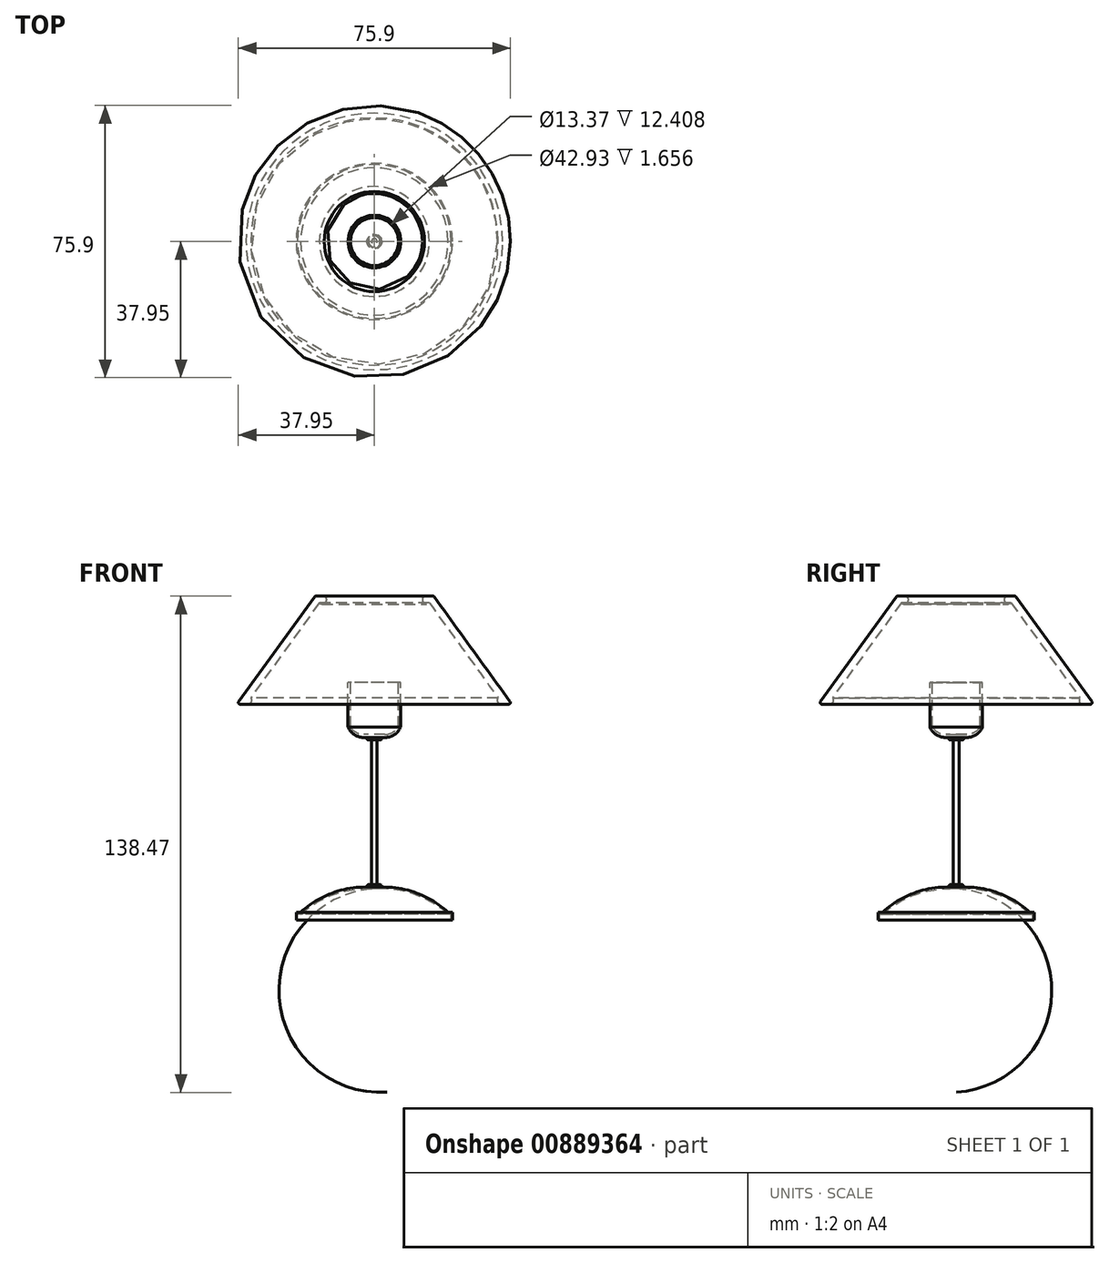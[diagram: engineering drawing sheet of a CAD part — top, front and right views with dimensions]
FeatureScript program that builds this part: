
annotation { "Feature Type Name" : "Feature", "Feature Type Description" : "" }
export const myFeature = defineFeature(function(context is Context, id is Id, definition is map)
    precondition{}
    {
        {
            var Q0;
            Q0=qCreatedBy(makeId("Front.planeOp"),FACE);
            var sketch = newSketch(context, id + "F0", { "sketchPlane" : qUnion([Q0])});
            skLineSegment(sketch, "E0", {"start": v(-13.97, 30.15) * mm, "end": v(-16.33, 30.15) * mm});
            skLineSegment(sketch, "E1", {"start": v(-16.7, 29.96) * mm, "end": v(-37.86, 0.73) * mm});
            skLineSegment(sketch, "E2", {"start": v(-37.48, 0) * mm, "end": v(-35.8, 0) * mm});
            skLineSegment(sketch, "E3", {"start": v(0, 30.15) * mm, "end": v(0, 37.7) * mm});
            skLineSegment(sketch, "E4", {"start": v(-34.51, 1.77) * mm, "end": v(-15.35, 28.25) * mm});
            skArc(sketch, "E5", {"start": v(-15.35, 28.25) * mm, "mid": v(-13.62, 28.45) * mm, "end": v(-13.97, 30.15) * mm});
            skArc(sketch, "E6", {"start": v(-35.8, 0) * mm, "mid": v(-34.5, 0.42) * mm, "end": v(-34.51, 1.77) * mm});
            skPoint(sketch, "E7.visualSharp", {"position": v(-38.39, 0) * mm});
            skArc(sketch, "E7.filletArc", {"start": v(-37.86, 0.73) * mm, "mid": v(-37.9, 0.25) * mm, "end": v(-37.48, 0) * mm});
            skPoint(sketch, "E8.visualSharp", {"position": v(-16.57, 30.15) * mm});
            skArc(sketch, "E8.filletArc", {"start": v(-16.33, 30.15) * mm, "mid": v(-16.54, 30.1) * mm, "end": v(-16.7, 29.96) * mm});
            skLineSegment(sketch, "E9", {"start": v(0, 0) * mm, "end": v(0, -60.18) * mm});
            skLineSegment(sketch, "E10", {"start": v(-21.47, -60.18) * mm, "end": v(-21.8, -60.18) * mm});
            skLineSegment(sketch, "E11", {"start": v(-21.8, -60.18) * mm, "end": v(-21.8, -58.08) * mm});
            skLineSegment(sketch, "E12", {"start": v(-21.8, -58.08) * mm, "end": v(-20.55, -58.08) * mm});
            skLineSegment(sketch, "E13", {"start": v(0, -51.02) * mm, "end": v(0, -51.5) * mm});
            skLineSegment(sketch, "E14", {"start": v(0, -51.02) * mm, "end": v(-2.49, -51.02) * mm});
            skArc(sketch, "E15", {"start": v(-2.49, -51.02) * mm, "mid": v(-12.18, -52.85) * mm, "end": v(-20.55, -58.08) * mm});
            skLineSegment(sketch, "E16", {"start": v(0, -50.3) * mm, "end": v(-1.58, -50.3) * mm});
            skArc(sketch, "E17", {"start": v(-1.58, -50.3) * mm, "mid": v(-1.94, -50.66) * mm, "end": v(-1.58, -51.02) * mm});
            skLineSegment(sketch, "E18", {"start": v(-0.79, -50.3) * mm, "end": v(-0.79, -9.98) * mm});
            skLineSegment(sketch, "E19", {"start": v(-0.79, -9.98) * mm, "end": v(-1.71, -9.98) * mm});
            skArc(sketch, "E20", {"start": v(-1.71, -9.28) * mm, "mid": v(-2.06, -9.63) * mm, "end": v(-1.71, -9.98) * mm});
            skLineSegment(sketch, "E21", {"start": v(-7.36, 6.1) * mm, "end": v(-7.36, -6.35) * mm});
            skArc(sketch, "E22", {"start": v(-7.36, -6.35) * mm, "mid": v(-5.58, -8.48) * mm, "end": v(-2.92, -9.28) * mm});
            skLineSegment(sketch, "E23", {"start": v(-7.36, 6.1) * mm, "end": v(-6.69, 6.1) * mm});
            skLineSegment(sketch, "E24", {"start": v(-6.69, 6.1) * mm, "end": v(-6.69, -6.31) * mm});
            skLineSegment(sketch, "E25", {"start": v(-2.92, -8.43) * mm, "end": v(0, -8.43) * mm});
            skArc(sketch, "E26", {"start": v(-6.69, -6.31) * mm, "mid": v(-5.08, -7.87) * mm, "end": v(-2.92, -8.43) * mm});
            skLineSegment(sketch, "E27.trimOffspring", {"start": v(-1.71, -9.28) * mm, "end": v(-2.92, -9.28) * mm});
            skLineSegment(sketch, "E28", {"start": v(-20.55, -58.53) * mm, "end": v(-21.47, -58.53) * mm});
            skLineSegment(sketch, "E29", {"start": v(-21.47, -58.53) * mm, "end": v(-21.47, -60.18) * mm});
            skLineSegment(sketch, "E30", {"start": v(0, -51.5) * mm, "end": v(0, -51.02) * mm});
            skArc(sketch, "E31", {"start": v(0, -51.5) * mm, "mid": v(-10.97, -52.98) * mm, "end": v(-20.55, -58.53) * mm});
            skSolve(sketch);
        }
        {
            var Q0;
            Q0=makeQuery(id+"F0.imprint","IMPRINT",FACE,{"disambiguationData":[TD([[makeQuery(id+"F0.imprint","IMPRINT",EDGE,{"derivedFrom":sQuery(id+"F0.wireOp",EDGE,"E0")}),1.0]])]});
            var Q1;
            {var subQ4=sQuery(id+"F0.wireOp",EDGE,"E18");Q1=makeQuery(id+"F0.imprint","IMPRINT",FACE,{"disambiguationData":[TD([[makeQuery(id+"F0.imprint","IMPRINT",EDGE,{"derivedFrom":subQ4}),-1.0]])]});}
            var Q2;
            {var subQ0=sQuery(id+"F0.wireOp",EDGE,"E17");Q2=makeQuery(id+"F0.imprint","IMPRINT",FACE,{"disambiguationData":[TD([[makeQuery(id+"F0.imprint","IMPRINT",EDGE,{"derivedFrom":subQ0}),1.0]])]});}
            var Q3;
            Q3=makeQuery(id+"F0.imprint","IMPRINT",FACE,{"disambiguationData":[TD([[makeQuery(id+"F0.imprint","IMPRINT",EDGE,{"derivedFrom":sQuery(id+"F0.wireOp",EDGE,"E10")}),-1.0]])]});
            var Q4;
            Q4=sQuery(id+"F0.wireOp",EDGE,"E9");
            revolve(context, id + "F1", {"surfaceOperationType" : NewSurfaceOperationType.NEW, "entities" : qUnion([Q0, Q1, Q2, Q3]), "axis" : qUnion([Q4]), "revolveType" : RevolveType.FULL});
        }
    });
